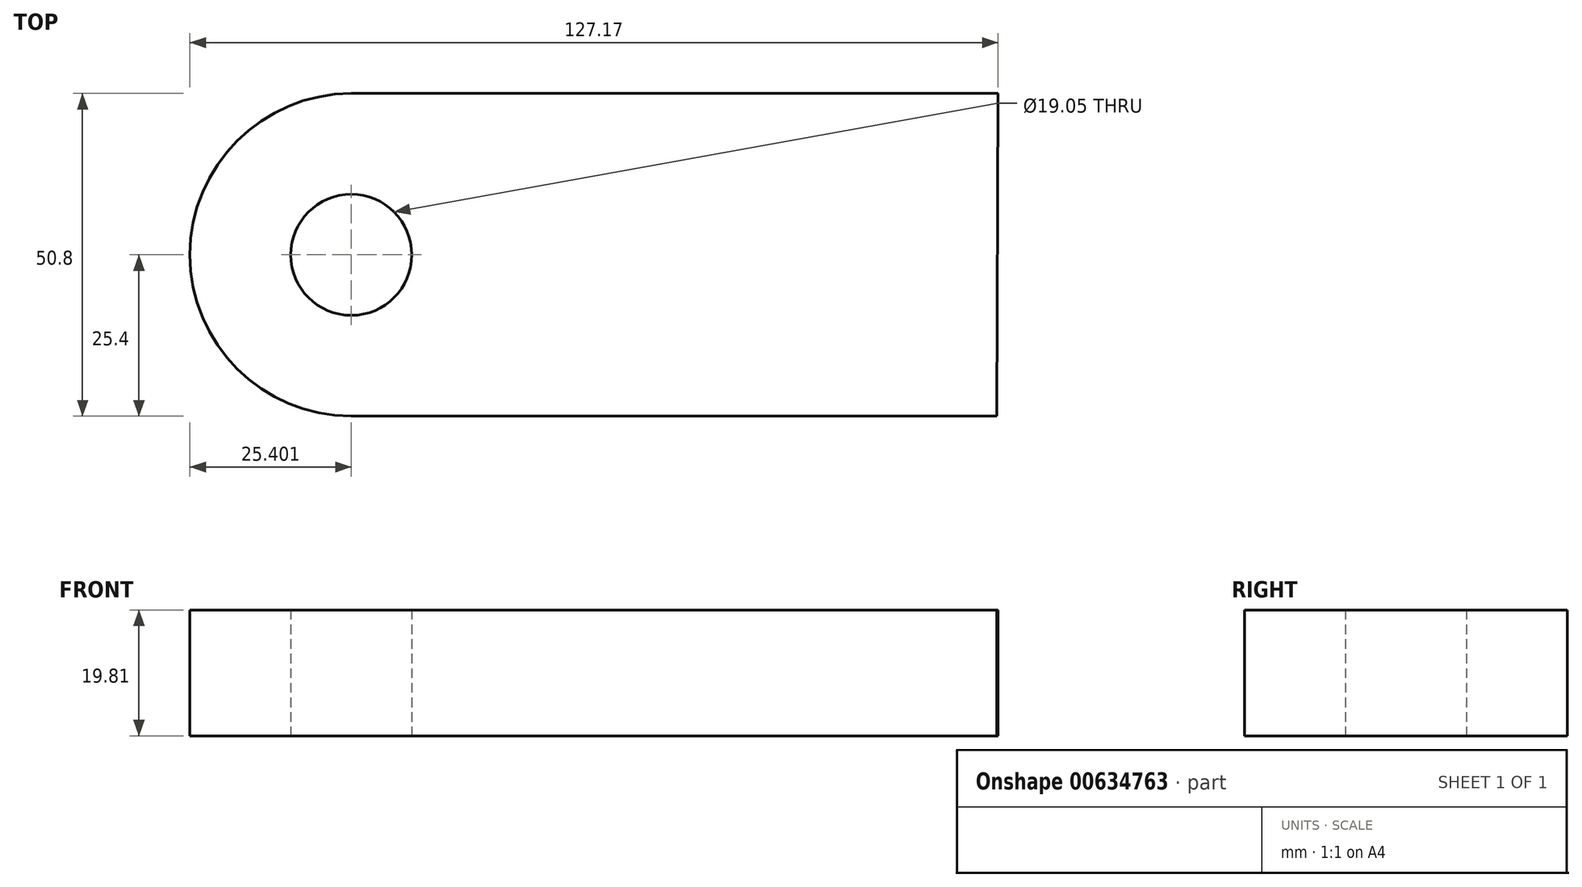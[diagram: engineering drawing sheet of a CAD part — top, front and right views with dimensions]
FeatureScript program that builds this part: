
annotation { "Feature Type Name" : "Feature", "Feature Type Description" : "" }
export const myFeature = defineFeature(function(context is Context, id is Id, definition is map)
    precondition{}
    {
        {
            var Q0;
            Q0=qCreatedBy(makeId("Top.planeOp"),FACE);
            var sketch = newSketch(context, id + "F0", { "sketchPlane" : qUnion([Q0])});
            skLineSegment(sketch, "E0", {"start": v(-50.52, 36.9) * mm, "end": v(51.25, 36.9) * mm});
            skLineSegment(sketch, "E1", {"start": v(-50.52, 36.9) * mm, "end": v(-50.52, -13.9) * mm});
            skLineSegment(sketch, "E2", {"start": v(-50.52, -13.9) * mm, "end": v(51.08, -13.9) * mm});
            skLineSegment(sketch, "E3", {"start": v(51.08, -13.9) * mm, "end": v(51.25, 36.9) * mm});
            skArc(sketch, "E4", {"start": v(-50.52, 36.9) * mm, "mid": v(-75.92, 11.5) * mm, "end": v(-50.52, -13.9) * mm});
            skCircle(sketch, "E5", {"center": v(-50.52, 11.5) * mm, "radius": 9.53 * mm});
            skSolve(sketch);
        }
        {
            var Q0;
            {var subQ0=sQuery(id+"F0.wireOp",EDGE,"E4");Q0=makeQuery(id+"F0.imprint","IMPRINT",FACE,{"disambiguationData":[TD([[makeQuery(id+"F0.imprint","IMPRINT",EDGE,{"derivedFrom":subQ0}),1.0]])]});}
            var Q1;
            {var subQ5=sQuery(id+"F0.wireOp",EDGE,"E0");Q1=makeQuery(id+"F0.imprint","IMPRINT",FACE,{"disambiguationData":[TD([[makeQuery(id+"F0.imprint","IMPRINT",EDGE,{"derivedFrom":subQ5}),-1.0]])]});}
            extrude(context, id + "F1", {"entities" : qUnion([Q0, Q1]), "depth" : 19.8 * mm, "offsetDistance" : 25.4 * mm});
        }
    });
